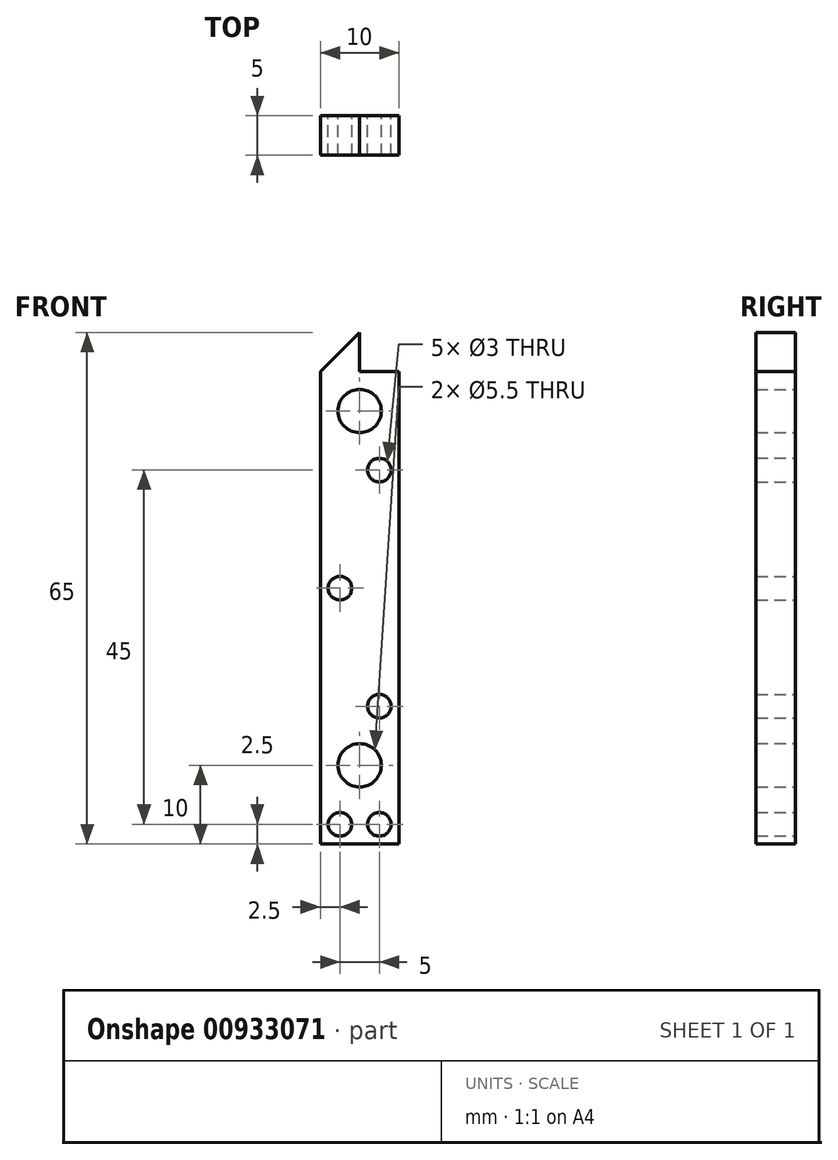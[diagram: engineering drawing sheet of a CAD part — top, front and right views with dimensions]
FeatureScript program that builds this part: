
annotation { "Feature Type Name" : "Feature", "Feature Type Description" : "" }
export const myFeature = defineFeature(function(context is Context, id is Id, definition is map)
    precondition{}
    {
        {
            var Q0;
            Q0=qCreatedBy(makeId("Front.planeOp"),FACE);
            var sketch = newSketch(context, id + "F0", { "sketchPlane" : qUnion([Q0])});
            skLineSegment(sketch, "E0.top", {"start": v(-5, -32.5) * mm, "end": v(5, -32.5) * mm});
            skLineSegment(sketch, "E0.left", {"start": v(-5, 27.5) * mm, "end": v(-5, -32.5) * mm});
            skLineSegment(sketch, "E0.right", {"start": v(5, 27.5) * mm, "end": v(5, -32.5) * mm});
            skPoint(sketch, "E0.middle", {"position": v(0, 0) * mm});
            skPoint(sketch, "E1", {"position": v(0, -22.5) * mm});
            skPoint(sketch, "E2", {"position": v(0, 22.5) * mm});
            skLineSegment(sketch, "E3", {"start": v(0, 32.5) * mm, "end": v(-5, 27.5) * mm});
            skLineSegment(sketch, "E4.top", {"start": v(0, 27.5) * mm, "end": v(5, 27.5) * mm});
            skLineSegment(sketch, "E4.left", {"start": v(0, 32.5) * mm, "end": v(0, 27.5) * mm});
            skCircle(sketch, "E5", {"center": v(0, 22.5) * mm, "radius": 2.75 * mm});
            skCircle(sketch, "E6", {"center": v(0, -22.5) * mm, "radius": 2.75 * mm});
            skPoint(sketch, "E7", {"position": v(2.5, 15) * mm});
            skPoint(sketch, "E8", {"position": v(-2.5, 0) * mm});
            skPoint(sketch, "E9", {"position": v(2.5, -15) * mm});
            skPoint(sketch, "E10", {"position": v(-2.5, -30) * mm});
            skPoint(sketch, "E11", {"position": v(2.5, -30) * mm});
            skCircle(sketch, "E12", {"center": v(2.5, 15) * mm, "radius": 1.5 * mm});
            skCircle(sketch, "E13", {"center": v(-2.5, 0) * mm, "radius": 1.5 * mm});
            skCircle(sketch, "E14", {"center": v(2.5, -15) * mm, "radius": 1.5 * mm});
            skCircle(sketch, "E15", {"center": v(-2.5, -30) * mm, "radius": 1.5 * mm});
            skCircle(sketch, "E16", {"center": v(2.5, -30) * mm, "radius": 1.5 * mm});
            skSolve(sketch);
        }
        {
            var Q0;
            Q0 = qSketchRegion(id + "F0", true);
            extrude(context, id + "F1", {"entities" : qUnion([Q0]), "depth" : 5 * mm, "offsetDistance" : 25 * mm});
        }
    });
